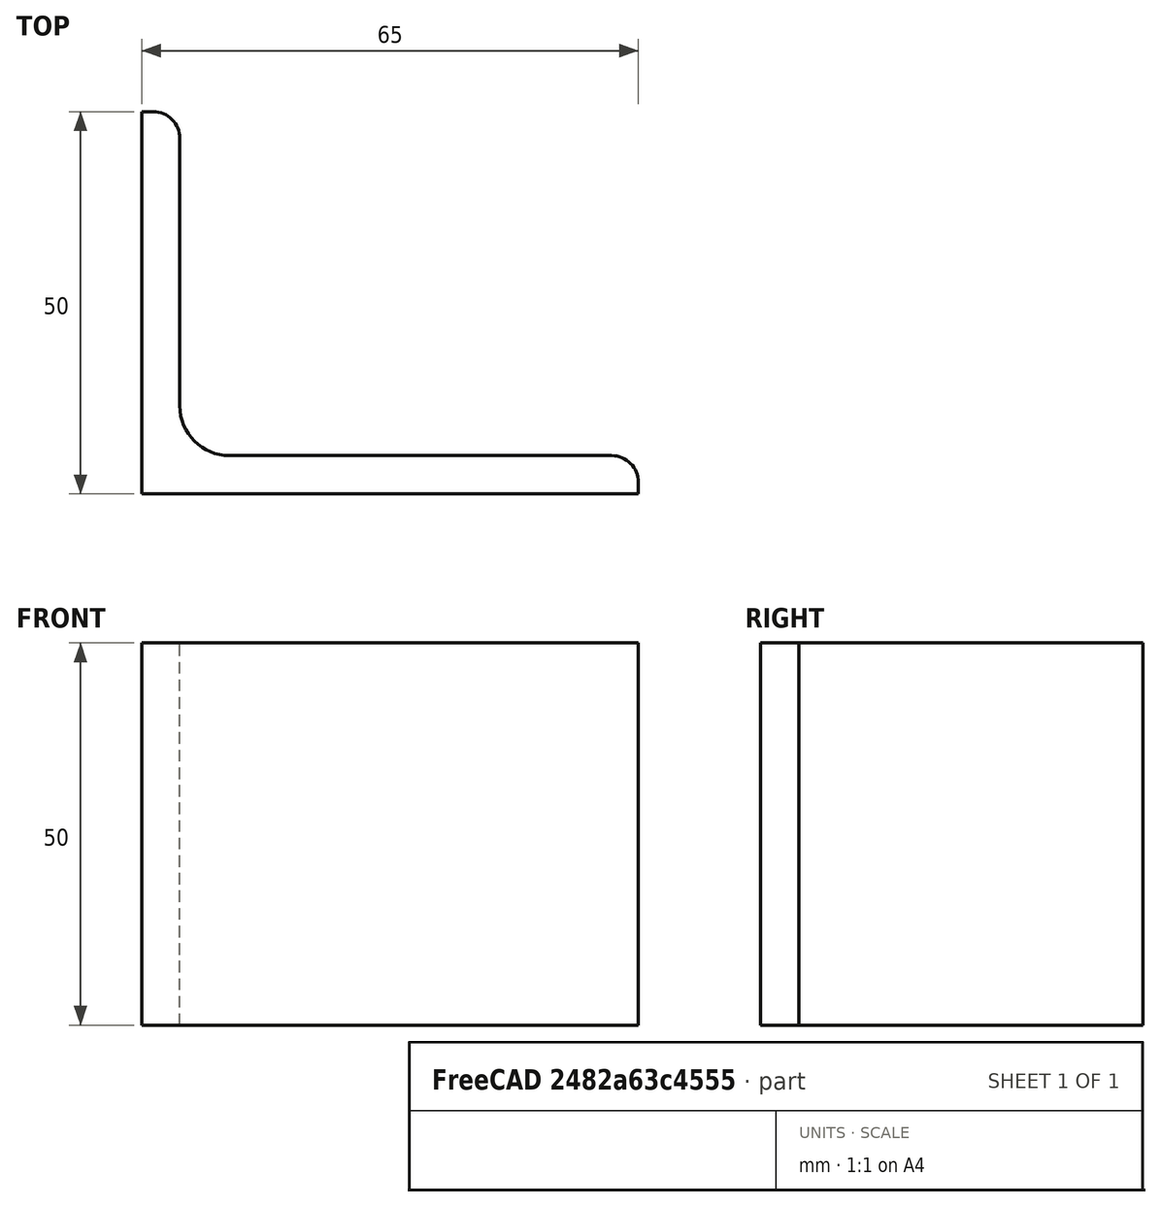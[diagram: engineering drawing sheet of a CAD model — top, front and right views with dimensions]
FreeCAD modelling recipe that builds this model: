
FCSTD DOCUMENT  (FreeCAD 0.15R4671 (Git))
Label: Angle Bar 65x50x5 EN10056 S235JR
License: All rights reserved
LicenseURL: http://en.wikipedia.org/wiki/All_rights_reserved
objects: Sketcher::SketchObject×1, Part::Extrusion×1
note: 2 computed .brp shape members not serialized (recipe doc carries the construction recipe); baked Part::Feature solids carry a one-line shape summary decoded from their .brp

FEATURE [Sketcher::SketchObject] Sketch
  sketch-geometry (9):
    g0: LineSegment StartX=0 StartY=0 StartZ=0 EndX=65 EndY=0 EndZ=0
    g1: LineSegment StartX=65 StartY=0 StartZ=0 EndX=65 EndY=1.5 EndZ=0
    g2: LineSegment StartX=61.5 StartY=5 StartZ=0 EndX=11.5 EndY=5 EndZ=0
    g3: LineSegment StartX=0 StartY=0 StartZ=0 EndX=0 EndY=50 EndZ=0
    g4: LineSegment StartX=0 StartY=50 StartZ=0 EndX=1.5 EndY=50 EndZ=0
    g5: LineSegment StartX=5 StartY=46.5 StartZ=0 EndX=5 EndY=11.5 EndZ=0
    g6: ArcOfCircle CenterX=11.5 CenterY=11.5 CenterZ=0 NormalX=0 NormalY=0 NormalZ=1 Radius=6.5 StartAngle=3.14159 EndAngle=4.71239
    g7: ArcOfCircle CenterX=1.5 CenterY=46.5 CenterZ=0 NormalX=0 NormalY=0 NormalZ=1 Radius=3.5 StartAngle=0 EndAngle=1.5708
    g8: ArcOfCircle CenterX=61.5 CenterY=1.5 CenterZ=0 NormalX=0 NormalY=0 NormalZ=1 Radius=3.5 StartAngle=0 EndAngle=1.5708
  constraints (23):
    c: Coincident(g0,g-1)
    c: Horizontal(g0)
    c: Coincident(g1,g0)
    c: Vertical(g1)
    c: Horizontal(g2)
    c: Coincident(g3,g-1)
    c: Vertical(g3)
    c: Coincident(g4,g3)
    c: Horizontal(g4)
    c: Vertical(g5)
    c: Tangent(g5,g6) = -1.5708
    c: Tangent(g2,g6) = 1.5708
    c: Tangent(g4,g7) = 1.5708
    c: Tangent(g5,g7) = 1.5708
    c: Tangent(g2,g8) = -1.5708
    c: Tangent(g1,g8) = -1.5708
    c: DistanceX(g0) = 65
    c: DistanceY(g3) = 50
    c: DistanceY(g0,g2) = 5
    c: DistanceX(g3,g5) = 5
    c: Radius(g6) = 6.5
    c: Radius(g8) = 3.5
    c: Radius(g7) = 3.5
FEATURE [Part::Extrusion] Extrude  label="Angle Bar 65x50x5 EN10056 S235JR"
  Base = -> Sketch
  Dir = (0,0,50)
  Solid = true
